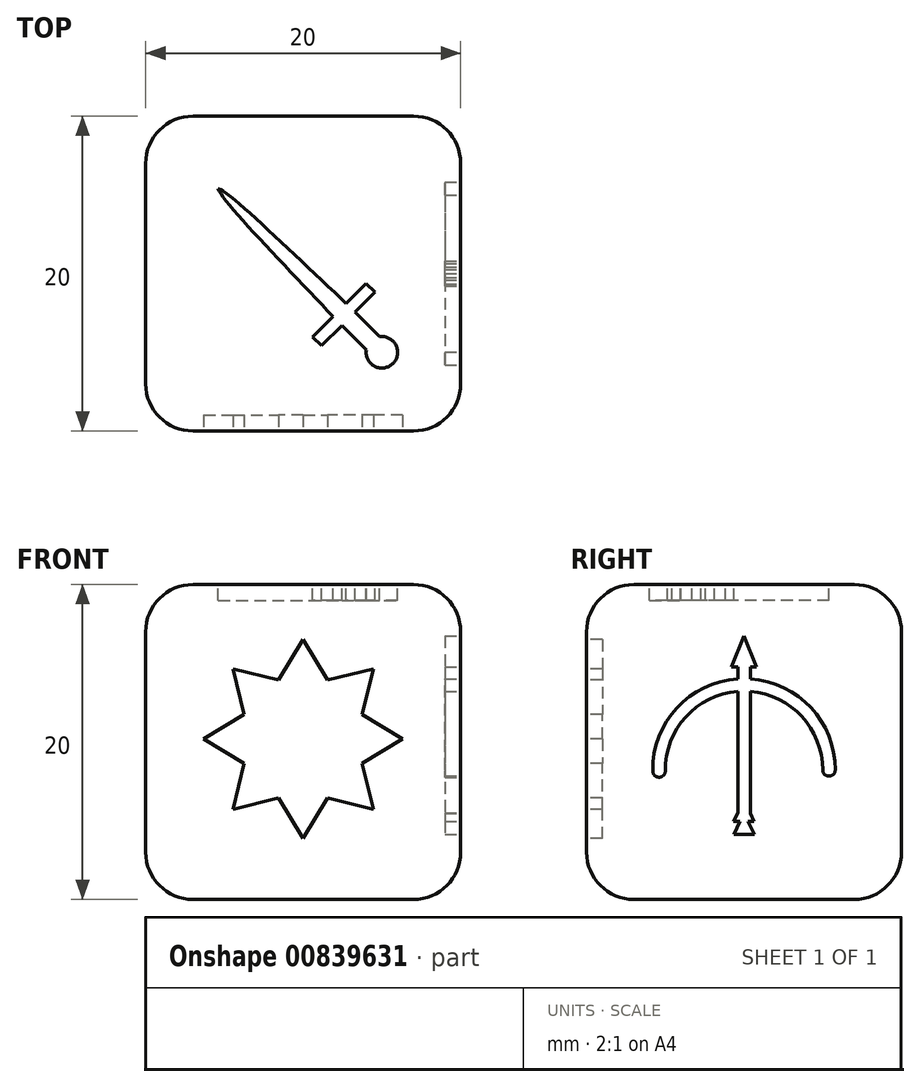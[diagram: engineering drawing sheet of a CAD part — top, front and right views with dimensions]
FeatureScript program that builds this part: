
annotation { "Feature Type Name" : "Feature", "Feature Type Description" : "" }
export const myFeature = defineFeature(function(context is Context, id is Id, definition is map)
    precondition{}
    {
        {
            var Q0;
            Q0=qCreatedBy(makeId("Front.planeOp"),FACE);
            var sketch = newSketch(context, id + "F0", { "sketchPlane" : qUnion([Q0])});
            skLineSegment(sketch, "E0.bottom", {"start": v(10, -10) * mm, "end": v(-10, -10) * mm});
            skLineSegment(sketch, "E0.top", {"start": v(10, 10) * mm, "end": v(-10, 10) * mm});
            skLineSegment(sketch, "E0.left", {"start": v(10, -10) * mm, "end": v(10, 10) * mm});
            skLineSegment(sketch, "E0.right", {"start": v(-10, -10) * mm, "end": v(-10, 10) * mm});
            skPoint(sketch, "E0.middle", {"position": v(0, 0) * mm});
            skSolve(sketch);
        }
        {
            var Q0;
            Q0 = qSketchRegion(id + "F0", true);
            extrude(context, id + "F1", {"entities" : qUnion([Q0]), "endBound" : BoundingType.SYMMETRIC, "depth" : 20 * mm, "offsetDistance" : 25 * mm});
        }
        {
            var Q0;
            Q0=makeQuery(id+"F1.opExtrude","CAP_EDGE",EDGE,{"disambiguationData":[OSD([sQuery(id+"F0.wireOp",EDGE,"E0.top")])],"isStart":false});
            var Q1;
            Q1=makeQuery(id+"F1.opExtrude","SWEPT_EDGE",EDGE,{"disambiguationData":[OSD([sQuery(id+"F0.wireOp",EDGE,"E0.top"),sQuery(id+"F0.wireOp",EDGE,"E0.left")])]});
            var Q2;
            Q2=makeQuery(id+"F1.opExtrude","SWEPT_FACE",FACE,{"disambiguationData":[OSD([sQuery(id+"F0.wireOp",EDGE,"E0.left")])]});
            var Q3;
            Q3=makeQuery(id+"F1.opExtrude","CAP_EDGE",EDGE,{"disambiguationData":[OSD([sQuery(id+"F0.wireOp",EDGE,"E0.bottom")])],"isStart":false});
            var Q4;
            Q4=makeQuery(id+"F1.opExtrude","CAP_EDGE",EDGE,{"disambiguationData":[OSD([sQuery(id+"F0.wireOp",EDGE,"E0.right")])],"isStart":false});
            var Q5;
            Q5=makeQuery(id+"F1.opExtrude","SWEPT_EDGE",EDGE,{"disambiguationData":[OSD([sQuery(id+"F0.wireOp",EDGE,"E0.bottom"),sQuery(id+"F0.wireOp",EDGE,"E0.right")])]});
            var Q6;
            Q6=makeQuery(id+"F1.opExtrude","CAP_EDGE",EDGE,{"disambiguationData":[OSD([sQuery(id+"F0.wireOp",EDGE,"E0.right")])],"isStart":true});
            var Q7;
            Q7=makeQuery(id+"F1.opExtrude","SWEPT_EDGE",EDGE,{"disambiguationData":[OSD([sQuery(id+"F0.wireOp",EDGE,"E0.top"),sQuery(id+"F0.wireOp",EDGE,"E0.right")])]});
            var Q8;
            Q8=makeQuery(id+"F1.opExtrude","CAP_EDGE",EDGE,{"disambiguationData":[OSD([sQuery(id+"F0.wireOp",EDGE,"E0.top")])],"isStart":true});
            var Q9;
            Q9=makeQuery(id+"F1.opExtrude","CAP_EDGE",EDGE,{"disambiguationData":[OSD([sQuery(id+"F0.wireOp",EDGE,"E0.bottom")])],"isStart":true});
            fillet(context, id + "F2", {"entities" : qUnion([Q0, Q1, Q2, Q3, Q4, Q5, Q6, Q7, Q8, Q9]), "radius" : 3 * mm, "tangentPropagation" : true, "allowEdgeOverflow" : false});
        }
        {
            var Q0;
            Q0=makeQuery(id+"F1.opExtrude","CAP_FACE",FACE,{"disambiguationData":[OSD([sQuery(id+"F0.wireOp",EDGE,"E0.bottom"),sQuery(id+"F0.wireOp",EDGE,"E0.top"),sQuery(id+"F0.wireOp",EDGE,"E0.left"),sQuery(id+"F0.wireOp",EDGE,"E0.right")])],"isStart":false});
            var sketch = newSketch(context, id + "F3", { "sketchPlane" : qUnion([Q0])});
            skLineSegment(sketch, "E1", {"start": v(0, 6.5) * mm, "end": v(-1.55, 3.93) * mm});
            skLineSegment(sketch, "E2.MirrorCS", {"start": v(0, 6.5) * mm, "end": v(1.55, 3.93) * mm});
            skLineSegment(sketch, "E3.1.0", {"start": v(-4.47, 4.65) * mm, "end": v(-3.75, 1.73) * mm});
            skLineSegment(sketch, "E3.1.1", {"start": v(-4.47, 4.65) * mm, "end": v(-1.55, 3.93) * mm});
            skLineSegment(sketch, "E3.2.0", {"start": v(-6.32, 0.18) * mm, "end": v(-3.75, -1.37) * mm});
            skLineSegment(sketch, "E3.2.1", {"start": v(-6.32, 0.18) * mm, "end": v(-3.75, 1.73) * mm});
            skLineSegment(sketch, "E3.3.0", {"start": v(-4.47, -4.28) * mm, "end": v(-1.55, -3.56) * mm});
            skLineSegment(sketch, "E3.3.1", {"start": v(-4.47, -4.28) * mm, "end": v(-3.75, -1.37) * mm});
            skLineSegment(sketch, "E3.4.0", {"start": v(0, -6.14) * mm, "end": v(1.55, -3.56) * mm});
            skLineSegment(sketch, "E3.4.1", {"start": v(0, -6.14) * mm, "end": v(-1.55, -3.56) * mm});
            skLineSegment(sketch, "E3.5.0", {"start": v(4.47, -4.28) * mm, "end": v(3.75, -1.37) * mm});
            skLineSegment(sketch, "E3.5.1", {"start": v(4.47, -4.28) * mm, "end": v(1.55, -3.56) * mm});
            skLineSegment(sketch, "E3.6.0", {"start": v(6.32, 0.18) * mm, "end": v(3.75, 1.73) * mm});
            skLineSegment(sketch, "E3.6.1", {"start": v(6.32, 0.18) * mm, "end": v(3.75, -1.37) * mm});
            skLineSegment(sketch, "E3.7.0", {"start": v(4.47, 4.65) * mm, "end": v(1.55, 3.93) * mm});
            skLineSegment(sketch, "E3.7.1", {"start": v(4.47, 4.65) * mm, "end": v(3.75, 1.73) * mm});
            skPoint(sketch, "E3.center", {"position": v(0, 0.18) * mm});
            skSolve(sketch);
        }
        {
            var Q0;
            Q0 = qSketchRegion(id + "F3", true);
            extrude(context, id + "F4", {"entities" : qUnion([Q0]), "operationType" : NewBodyOperationType.REMOVE, "oppositeDirection" : true, "depth" : 1 * mm, "offsetDistance" : 25 * mm});
        }
        {
            var Q0;
            Q0=makeQuery(id+"F1.opExtrude","SWEPT_FACE",FACE,{"disambiguationData":[OSD([sQuery(id+"F0.wireOp",EDGE,"E0.left")])]});
            var sketch = newSketch(context, id + "F5", { "sketchPlane" : qUnion([Q0])});
            skArc(sketch, "E4", {"start": v(-5.8, -1.85) * mm, "mid": v(-0.04, 4.02) * mm, "end": v(5.8, -1.77) * mm});
            skArc(sketch, "E5.0", {"start": v(-5, -1.84) * mm, "mid": v(-0.03, 3.22) * mm, "end": v(5, -1.77) * mm});
            skArc(sketch, "E6", {"start": v(-5.8, -1.85) * mm, "mid": v(-5.4, -2.24) * mm, "end": v(-5, -1.84) * mm});
            skArc(sketch, "E7", {"start": v(5, -1.77) * mm, "mid": v(5.4, -2.17) * mm, "end": v(5.8, -1.77) * mm});
            skLineSegment(sketch, "E8", {"start": v(0.4, 4.77) * mm, "end": v(0.4, -4.55) * mm});
            skLineSegment(sketch, "E9", {"start": v(0, 6.72) * mm, "end": v(-0.8, 4.77) * mm});
            skLineSegment(sketch, "E10.MirrorCS", {"start": v(0, 6.72) * mm, "end": v(0.8, 4.77) * mm});
            skLineSegment(sketch, "E11", {"start": v(-0.8, 4.77) * mm, "end": v(0.8, 4.77) * mm});
            skLineSegment(sketch, "E12", {"start": v(0, -4.5) * mm, "end": v(-0.65, -5.88) * mm});
            skLineSegment(sketch, "E13.MirrorCS", {"start": v(0, -4.5) * mm, "end": v(0.65, -5.88) * mm});
            skLineSegment(sketch, "E14", {"start": v(-0.65, -5.88) * mm, "end": v(0.65, -5.88) * mm});
            skLineSegment(sketch, "E15", {"start": v(0, -3.72) * mm, "end": v(-0.66, -5.04) * mm});
            skLineSegment(sketch, "E16.MirrorCS", {"start": v(0, -3.72) * mm, "end": v(0.64, -5.04) * mm});
            skLineSegment(sketch, "E17", {"start": v(-0.66, -5.04) * mm, "end": v(0.64, -5.04) * mm});
            skLineSegment(sketch, "E18.0", {"start": v(-0.4, 4.77) * mm, "end": v(-0.4, -4.51) * mm});
            skSolve(sketch);
        }
        {
            var Q0;
            Q0 = qSketchRegion(id + "F5", true);
            extrude(context, id + "F6", {"entities" : qUnion([Q0]), "operationType" : NewBodyOperationType.REMOVE, "oppositeDirection" : true, "depth" : 1 * mm, "offsetDistance" : 25 * mm});
        }
        {
            var Q0;
            Q0=makeQuery(id+"F1.opExtrude","SWEPT_FACE",FACE,{"disambiguationData":[OSD([sQuery(id+"F0.wireOp",EDGE,"E0.top")])]});
            var sketch = newSketch(context, id + "F7", { "sketchPlane" : qUnion([Q0])});
            skLineSegment(sketch, "E19", {"start": v(-5.4, 5.4) * mm, "end": v(5, -5) * mm});
            skLineSegment(sketch, "E20", {"start": v(4.58, -1.18) * mm, "end": v(1.18, -4.58) * mm});
            skLineSegment(sketch, "E21.0", {"start": v(3.99, -0.64) * mm, "end": v(0.6, -4.03) * mm});
            skLineSegment(sketch, "E22", {"start": v(0.6, -4.03) * mm, "end": v(1.18, -4.58) * mm});
            skLineSegment(sketch, "E23", {"start": v(3.99, -0.64) * mm, "end": v(4.58, -1.18) * mm});
            skFitSpline(sketch, "E24", {"points": [v(-5.4, 5.4) * mm, v(2.74, -1.89) * mm], "startDerivative": vector(2.9, -0.95) * mm, "endDerivative": vector(8.34, -7.61) * mm});
            skFitSpline(sketch, "E25.MirrorCS", {"points": [v(-5.4, 5.4) * mm, v(1.89, -2.74) * mm], "startDerivative": vector(0.95, -2.9) * mm, "endDerivative": vector(7.61, -8.34) * mm});
            skCircle(sketch, "E26", {"center": v(5, -5) * mm, "radius": 1 * mm});
            skLineSegment(sketch, "E27", {"start": v(2.45, -3.3) * mm, "end": v(4.01, -4.86) * mm});
            skLineSegment(sketch, "E28.MirrorCS", {"start": v(3.3, -2.45) * mm, "end": v(4.86, -4.01) * mm});
            skLineSegment(sketch, "E29", {"start": v(4.01, -4.86) * mm, "end": v(4.86, -4.01) * mm});
            skSolve(sketch);
        }
        {
            var Q0;
            Q0 = qSketchRegion(id + "F7", true);
            extrude(context, id + "F8", {"entities" : qUnion([Q0]), "operationType" : NewBodyOperationType.REMOVE, "oppositeDirection" : true, "depth" : 1 * mm, "offsetDistance" : 25 * mm});
        }
    });
